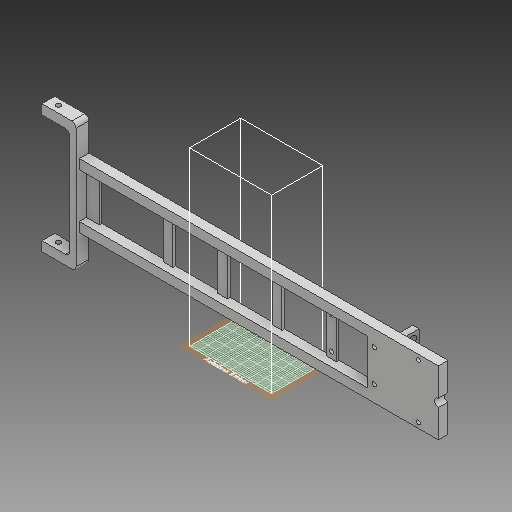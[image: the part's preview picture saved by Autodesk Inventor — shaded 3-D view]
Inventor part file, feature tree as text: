
AUTODESK INVENTOR PART (.ipt)
format: ipt  version: 2018 (Build 220112000, 112)  size: 615,936 bytes
history: native  units: mm
features: sketch x34, extrude x26, hole x6, fillet x6
ambient origin geometry x8: Origin, YZ Plane, XZ Plane, XY Plane, X Axis, Y Axis, Z Axis, Center Point
bodies: Solid1 (feature_tree)
feature tree (72):
  extrude  "Extrusion1"  Depth=50.0mm
  hole  "Hole1"  [1 undecoded]
  hole  "Hole2"  [1 undecoded]
  extrude  "Extrusion2"  Depth=25.0mm
  extrude  "Extrusion3"  Depth=25.0mm
  extrude  "Extrusion4"  Depth=5.0mm
  sketch  "Sketch7"  dims[d25=10.0mm d26=5.0mm]
  extrude  "Extrusion5"  Depth=5.0mm
  extrude  "Extrusion6"  Depth=35.0mm
  extrude  "Extrusion7"  Depth=35.0mm
  extrude  "Extrusion8"  Depth=35.0mm
  extrude  "Extrusion9"  Depth=2.0mm TaperAngle=0.0deg
  extrude  "Extrusion10"  Depth=7.5mm TaperAngle=0.0deg
  extrude  "Extrusion11"  Depth=10.0mm
  extrude  "Extrusion12"  Depth=7.5mm
  fillet  "Fillet1"  Radius=7.5mm
  fillet  "Fillet2"  Radius=25.0mm
  fillet  "Fillet3"  Radius=3.0mm
  fillet  "Fillet4"  Radius=3.2mm
  fillet  "Fillet5"  Radius=2.1mm
  fillet  "Fillet6"  Radius=5.5mm
  extrude  "Extrusion13"  Depth=92.5mm TaperAngle=0.0deg
  sketch  "Sketch17"  dims[d58=4.25mm d59=241.0mm d60=0.0mm]
  hole  "Hole3"  [1 undecoded]
  hole  "Hole4"  [1 undecoded]
  extrude  "Extrusion14"  Depth=5.0mm
  extrude  "Extrusion15"  Depth=2.5mm TaperAngle=0.0deg
  extrude  "Extrusion16"  Depth=6.35mm
  extrude  "Extrusion17"  Depth=2.5mm
  extrude  "Extrusion18"  Depth=14.55mm TaperAngle=0.0deg
  extrude  "Extrusion19"  Depth=0.1mm
  extrude  "Extrusion20"  Depth=3.25mm
  extrude  "Extrusion21"  Depth=3.25mm
  hole  "Hole5"  [1 undecoded]
  extrude  "Extrusion22"  Depth=2.0mm
  extrude  "Extrusion23"  Depth=15.0mm
  extrude  "Extrusion24"  Depth=10.0mm TaperAngle=0.0deg
  hole  "Hole6"  [1 undecoded]
  extrude  "Extrusion25"  Depth=100.0mm TaperAngle=0.0deg
  extrude  "Extrusion26"  Depth=2.0mm TaperAngle=0.0deg
  sketch  "Sketch1"  dims[d0=50.0mm d1=50.0mm]
  sketch  "Sketch2"  dims[d2=240.0mm d3=7.5mm]
  sketch  "Sketch3"  dims[d4=7.5mm d5=7.5mm d6=0.0mm]
  sketch  "Sketch4"  dims[d7=6.35mm d8=6.0mm d9=4.0mm d10=2.0mm d11=90.0deg d12=8.0mm d13=20.594885mm d14=25.0mm]
  sketch  "Sketch5"  dims[d15=3.3mm d16=6.0mm d17=4.0mm d18=2.0mm d19=90.0deg d20=8.0mm d21=20.594885mm d22=25.0mm]
  sketch  "Sketch6"  dims[d23=180.0deg d24=5.0mm]
  sketch  "Sketch8"  dims[d27=17.5mm d28=0.0mm d30=35.0mm]
  sketch  "Sketch9"  dims[d31=35.0mm d32=35.0mm]
  sketch  "Sketch10"  dims[d33=35.0mm d34=35.0mm]
  sketch  "Sketch11"  dims[d35=35.0mm d36=2.0mm d37=0.0mm]
  sketch  "Sketch12"  dims[d38=10.0mm d39=7.5mm d40=0.0mm]
  sketch  "Sketch13"  dims[d41=100.0mm d42=10.0mm]
  sketch  "Sketch14"  dims[d43=7.5mm d44=0.0mm d45=7.5mm d46=7.5mm d47=25.0mm d48=0.0mm d49=3.0mm d50=3.2mm d51=2.1mm d52=5.5mm]
  sketch  "Sketch15"  dims[d53=3.3mm d54=92.5mm d55=0.0mm]
  sketch  "Sketch16"  dims[d56=5.5mm d57=3.3mm]
  sketch  "Sketch18"  dims[d61=4.44mm d62=5.0mm]
  sketch  "Sketch19"  dims[d63=2.5mm d64=91.25mm d65=0.0mm]
  sketch  "Sketch20"  dims[d66=30.0mm d67=6.35mm]
  sketch  "Sketch21"  dims[d68=3.8mm d69=0.0mm d70=2.5mm]
  sketch  "Sketch22"  dims[d71=14.55mm d72=0.0mm d73=14.55mm d74=0.0mm]
  sketch  "Sketch23"  dims[d75=0.1mm d76=0.1mm]
  sketch  "Sketch24"  dims[d77=3.25mm d78=3.25mm]
  sketch  "Sketch25"  dims[d79=3.25mm d80=3.25mm]
  sketch  "Sketch26"  dims[d81=35.0mm d82=10.0mm]
  sketch  "Sketch27"  dims[d83=2.0mm d84=0.0mm d85=3.6mm]
  sketch  "Sketch28"  dims[d86=3.6mm]
  sketch  "Sketch29"  dims[d87=3.3mm d88=6.0mm d89=4.0mm d90=2.0mm d91=90.0deg d92=15.0mm d93=20.594885mm]
  sketch  "Sketch30"  dims[d94=3.3mm d95=6.0mm d96=4.0mm d97=2.0mm d98=90.0deg d99=15.0mm d100=20.594885mm d101=6.0mm]
  sketch  "Sketch31"  dims[d102=20.0mm d103=0.0mm d104=10.0mm d105=0.0mm]
  sketch  "Sketch32"  dims[d106=2.0mm d107=0.0mm d108=4.0mm]
  sketch  "Sketch33"  dims[d109=100.0mm d110=0.0mm d111=100.0mm d112=0.0mm]
  sketch  "Sketch34"  dims[d113=5.0mm d114=2.0mm d115=0.0mm d116=3.3mm d117=3.3mm d118=3.3mm d119=3.3mm d120=2.0mm d121=0.0mm d122=5.5mm d123=0.0mm d124=3.3mm d125=6.0mm d126=4.0mm d127=2.0mm d128=90.0deg d129=8.0mm d130=20.594885mm d131=42.0mm d132=17.0mm d133=21.0mm d135=8.5mm d136=15.825mm d137=3.5mm d138=21.0mm d139=3.3mm d140=3.3mm d141=3.3mm d142=10.0mm d143=0.0mm d144=7.5mm d145=0.0mm d146=100.0mm d147=0.0mm d148=5.0mm d149=6.0mm d150=4.0mm d151=2.0mm d152=90.0deg d153=15.0mm d154=0.0mm d155=3.75mm d156=100.0mm d157=0.0mm d158=100.0mm d159=0.0mm]
note: 6 required parameter values undecoded (feature->parameter linkage not recoverable at this tier; creation-order binding heuristic only, values carry confidence <= 0.55)
